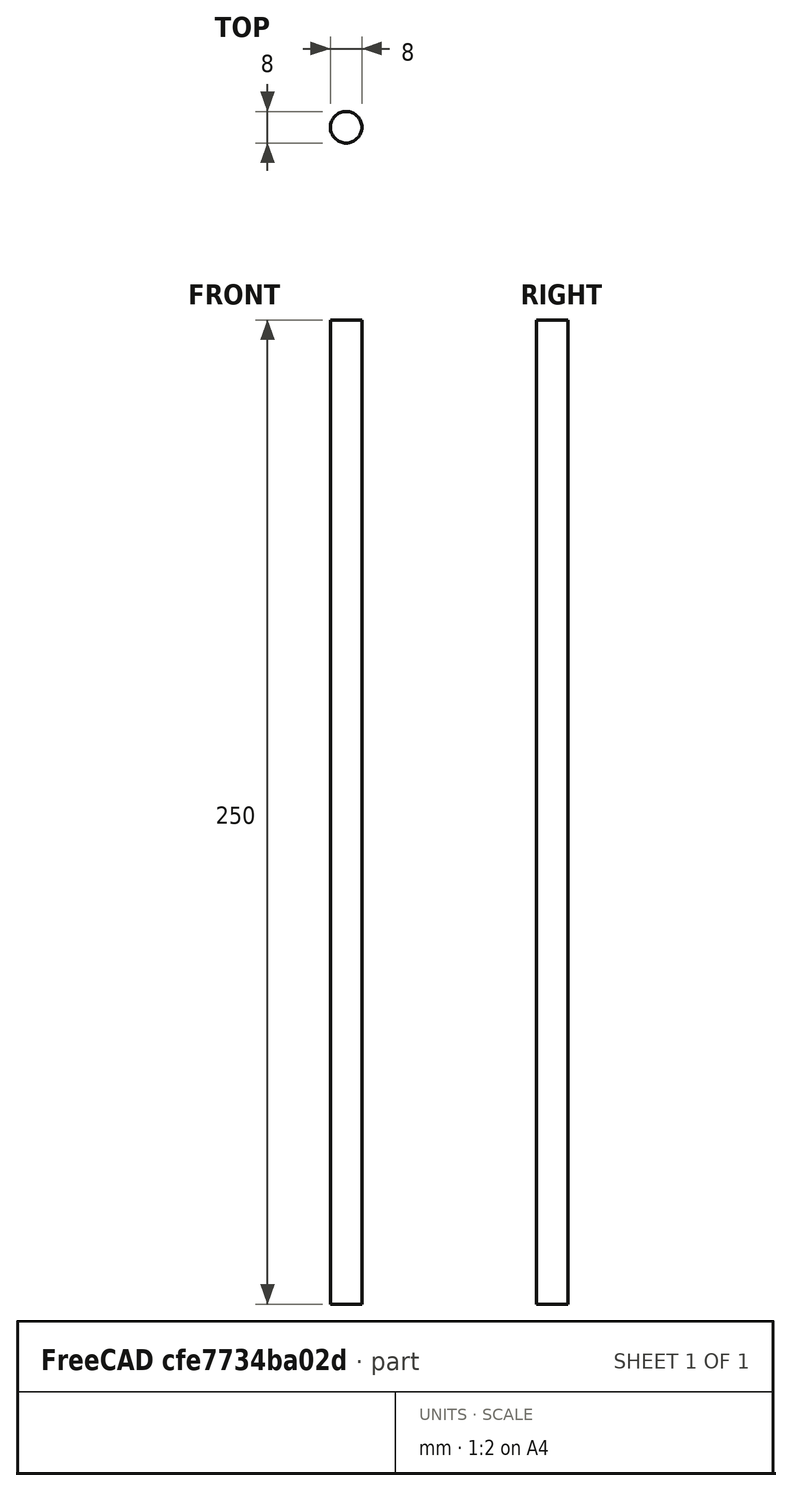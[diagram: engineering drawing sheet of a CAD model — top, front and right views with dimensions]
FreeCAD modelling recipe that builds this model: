
FCSTD DOCUMENT  (FreeCAD 0.19R22960 (Git))
Label: 500mm_Rail
License: All rights reserved
LicenseURL: http://en.wikipedia.org/wiki/All_rights_reserved
objects: Sketcher::SketchObject×1, PartDesign::Pad×1, PartDesign::Body×1, App::DocumentObjectGroup×1, App::FeaturePython×1, PartDesign::CoordinateSystem×1, App::Part×1
note: 5 computed .brp shape members not serialized (recipe doc carries the construction recipe); baked Part::Feature solids carry a one-line shape summary decoded from their .brp

FEATURE [Sketcher::SketchObject] Sketch
  MapMode = 5
  Support = -> [XY_Plane]
  sketch-geometry (1):
    g0: Circle CenterX=0 CenterY=0 CenterZ=0 NormalX=0 NormalY=0 NormalZ=1 AngleXU=0 Radius=4
  constraints (2):
    c: Coincident(g-1,g0)
    c: Radius(g0) = 4
FEATURE [PartDesign::Pad] Pad
  AllowMultiFace = false
  Direction = (1,1,1)
  Length = 250
  Length2 = 100
  Profile = -> Sketch
  Type = 0
FEATURE [PartDesign::Body] Body
  Group = -> [Sketch,Pad]
  Origin = -> Origin
  Placement = pos=(0,0,-53) rot=(0,0,1;0rad)
  Tip = -> Pad
FEATURE [App::DocumentObjectGroup] Constraints
FEATURE [App::FeaturePython] Variables  # WARN: FeaturePython — macro-defined, semantics opaque (R4)
FEATURE [PartDesign::CoordinateSystem] Center
  AttacherType = Attacher::AttachEngine3D
FEATURE [App::Part] Model
  Configuration = 0
  Group = -> [Constraints,Variables,Body,Center]
  Origin = -> Origin001
  Type = Assembly4 Model
